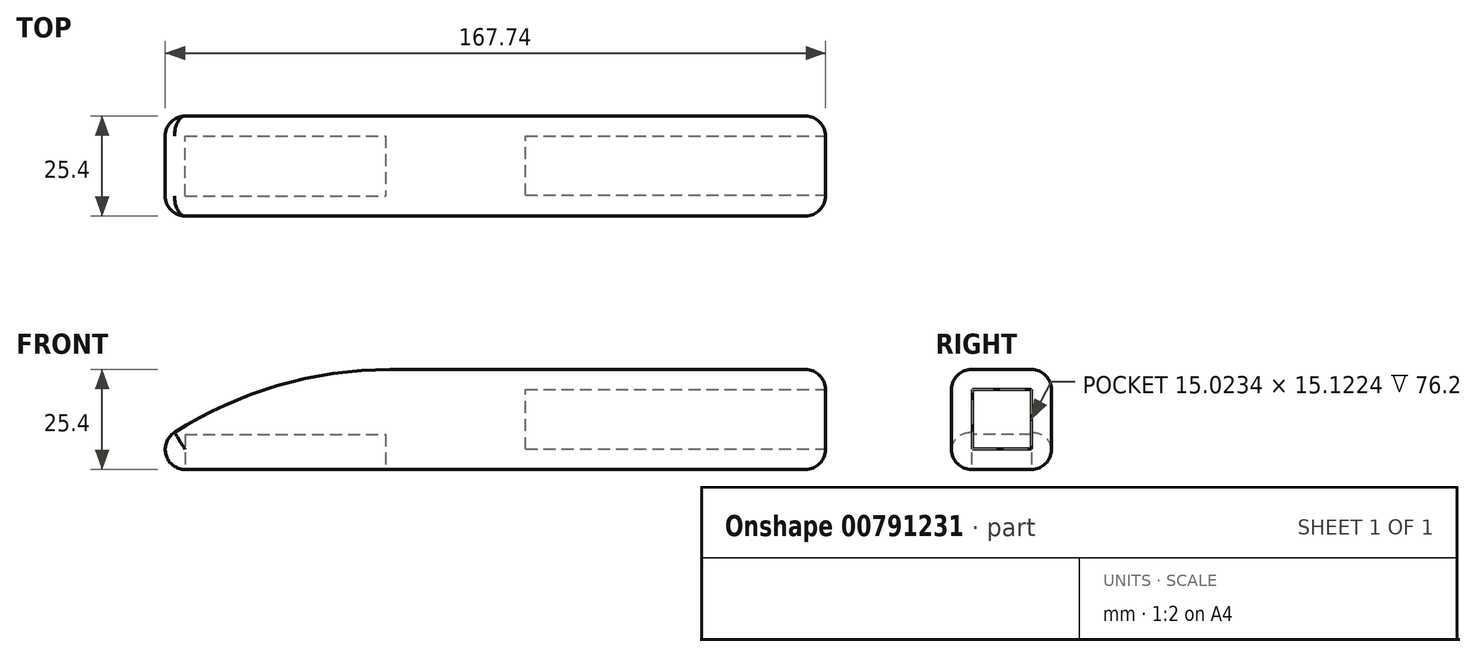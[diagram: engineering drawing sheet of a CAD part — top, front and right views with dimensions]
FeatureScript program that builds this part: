
annotation { "Feature Type Name" : "Feature", "Feature Type Description" : "" }
export const myFeature = defineFeature(function(context is Context, id is Id, definition is map)
    precondition{}
    {
        {
            var Q0;
            Q0=qCreatedBy(makeId("Top.planeOp"),FACE);
            var sketch = newSketch(context, id + "F0", { "sketchPlane" : qUnion([Q0])});
            skLineSegment(sketch, "E0.bottom", {"start": v(-85.74, 12.7) * mm, "end": v(92.06, 12.7) * mm});
            skLineSegment(sketch, "E0.top", {"start": v(-85.74, -12.7) * mm, "end": v(92.06, -12.7) * mm});
            skLineSegment(sketch, "E0.left", {"start": v(-85.74, 12.7) * mm, "end": v(-85.74, -12.7) * mm});
            skLineSegment(sketch, "E0.right", {"start": v(92.06, 12.7) * mm, "end": v(92.06, -12.7) * mm});
            skPoint(sketch, "E0.middle", {"position": v(3.16, 0) * mm});
            skSolve(sketch);
        }
        {
            var Q0;
            Q0=makeQuery(id+"F0.imprint","IMPRINT",FACE,{"disambiguationData":[TD([[makeQuery(id+"F0.imprint","IMPRINT",EDGE,{"derivedFrom":sQuery(id+"F0.wireOp",EDGE,"E0.bottom")}),-1.0]])]});
            extrude(context, id + "F1", {"entities" : qUnion([Q0]), "depth" : 25.4 * mm, "offsetDistance" : 25.4 * mm});
        }
        {
            var Q0;
            Q0=makeQuery(id+"F1.opExtrude","CAP_EDGE",EDGE,{"disambiguationData":[OSD([sQuery(id+"F0.wireOp",EDGE,"E0.left")])],"isStart":false});
            fillet(context, id + "F2", {"entities" : qUnion([Q0]), "radius" : 101.6 * mm, "tangentPropagation" : true, "allowEdgeOverflow" : false});
        }
        {
            var Q0;
            Q0=makeQuery(id+"F2.opFillet","BLEND_EDGE",EDGE,{"blendedFrom":[makeQuery(id+"F1.opExtrude","CAP_EDGE",EDGE,{"disambiguationData":[OSD([sQuery(id+"F0.wireOp",EDGE,"E0.left")])],"isStart":false}),makeQuery(id+"F1.opExtrude","SWEPT_FACE",FACE,{"disambiguationData":[OSD([sQuery(id+"F0.wireOp",EDGE,"E0.top")])]})],"blendedInto":[makeQuery(id+"F1.opExtrude","SWEPT_FACE",FACE,{"disambiguationData":[OSD([sQuery(id+"F0.wireOp",EDGE,"E0.top")])]})]});
            var Q1;
            Q1=makeQuery(id+"F2.opFillet","BLEND_EDGE",EDGE,{"blendedFrom":[makeQuery(id+"F1.opExtrude","CAP_EDGE",EDGE,{"disambiguationData":[OSD([sQuery(id+"F0.wireOp",EDGE,"E0.left")])],"isStart":false}),makeQuery(id+"F1.opExtrude","SWEPT_FACE",FACE,{"disambiguationData":[OSD([sQuery(id+"F0.wireOp",EDGE,"E0.bottom")])]})],"blendedInto":[makeQuery(id+"F1.opExtrude","SWEPT_FACE",FACE,{"disambiguationData":[OSD([sQuery(id+"F0.wireOp",EDGE,"E0.bottom")])]})]});
            fillet(context, id + "F3", {"entities" : qUnion([Q0, Q1]), "radius" : 5.08 * mm, "tangentPropagation" : true, "allowEdgeOverflow" : false});
        }
        {
            var Q0;
            Q0=makeQuery(id+"F1.opExtrude","SWEPT_FACE",FACE,{"disambiguationData":[OSD([sQuery(id+"F0.wireOp",EDGE,"E0.right")])]});
            var sketch = newSketch(context, id + "F4", { "sketchPlane" : qUnion([Q0])});
            skLineSegment(sketch, "E1.bottom", {"start": v(-7.4, 5.2) * mm, "end": v(7.62, 5.2) * mm});
            skLineSegment(sketch, "E1.top", {"start": v(-7.4, 20.32) * mm, "end": v(7.62, 20.32) * mm});
            skLineSegment(sketch, "E1.left", {"start": v(-7.4, 5.2) * mm, "end": v(-7.4, 20.32) * mm});
            skLineSegment(sketch, "E1.right", {"start": v(7.62, 5.2) * mm, "end": v(7.62, 20.32) * mm});
            skSolve(sketch);
        }
        {
            var Q0;
            Q0=makeQuery(id+"F4.imprint","IMPRINT",FACE,{"disambiguationData":[TD([[makeQuery(id+"F4.imprint","IMPRINT",EDGE,{"derivedFrom":sQuery(id+"F4.wireOp",EDGE,"E1.bottom")}),1.0]])]});
            extrude(context, id + "F5", {"entities" : qUnion([Q0]), "operationType" : NewBodyOperationType.REMOVE, "oppositeDirection" : true, "depth" : 76.2 * mm, "offsetDistance" : 25.4 * mm});
        }
        {
            var Q0;
            Q0=makeQuery(id+"F1.opExtrude","CAP_EDGE",EDGE,{"disambiguationData":[OSD([sQuery(id+"F0.wireOp",EDGE,"E0.right")])],"isStart":false});
            var Q1;
            Q1=makeQuery(id+"F1.opExtrude","CAP_EDGE",EDGE,{"disambiguationData":[OSD([sQuery(id+"F0.wireOp",EDGE,"E0.right")])],"isStart":true});
            fillet(context, id + "F6", {"entities" : qUnion([Q0, Q1]), "radius" : 5.08 * mm, "tangentPropagation" : true, "allowEdgeOverflow" : false});
        }
        {
            var Q0;
            Q0=makeQuery(id+"F1.opExtrude","CAP_EDGE",EDGE,{"disambiguationData":[OSD([sQuery(id+"F0.wireOp",EDGE,"E0.top")])],"isStart":true});
            var Q1;
            Q1=makeQuery(id+"F1.opExtrude","CAP_EDGE",EDGE,{"disambiguationData":[OSD([sQuery(id+"F0.wireOp",EDGE,"E0.bottom")])],"isStart":true});
            fillet(context, id + "F7", {"entities" : qUnion([Q0, Q1]), "radius" : 5.08 * mm, "tangentPropagation" : true, "allowEdgeOverflow" : false});
        }
        {
            var Q0;
            Q0=makeQuery(id+"F1.opExtrude","CAP_FACE",FACE,{"disambiguationData":[OSD([sQuery(id+"F0.wireOp",EDGE,"E0.bottom"),sQuery(id+"F0.wireOp",EDGE,"E0.top"),sQuery(id+"F0.wireOp",EDGE,"E0.left"),sQuery(id+"F0.wireOp",EDGE,"E0.right")])],"isStart":true});
            var sketch = newSketch(context, id + "F8", { "sketchPlane" : qUnion([Q0])});
            skLineSegment(sketch, "E2", {"start": v(-19.69, -7.62) * mm, "end": v(-19.69, 7.62) * mm});
            skSolve(sketch);
        }
        {
            var Q0;
            {var subQ0=sQuery(id+"F8.wireOp",EDGE,"E2");Q0=makeQuery(id+"F8.imprint","IMPRINT",FACE,{"disambiguationData":[TD([[makeQuery(id+"F8.imprint","IMPRINT",EDGE,{"derivedFrom":subQ0}),1.0]])]});}
            extrude(context, id + "F9", {"entities" : qUnion([Q0]), "operationType" : NewBodyOperationType.REMOVE, "oppositeDirection" : true, "depth" : 8.9 * mm, "offsetDistance" : 25.4 * mm});
        }
        {
            var Q0;
            Q0=makeQuery(id+"F1.opExtrude","SWEPT_FACE",FACE,{"disambiguationData":[OSD([sQuery(id+"F0.wireOp",EDGE,"E0.top")])]});
            var sketch = newSketch(context, id + "F10", { "sketchPlane" : qUnion([Q0])});
            skLineSegment(sketch, "E3", {"start": v(-30.42, 18.15) * mm, "end": v(-30.42, 7.54) * mm});
            skLineSegment(sketch, "E4", {"start": v(-25.14, 18.15) * mm, "end": v(-25.14, 13.62) * mm});
            skLineSegment(sketch, "E5", {"start": v(-25.14, 13.62) * mm, "end": v(-30.42, 13.62) * mm});
            skSolve(sketch);
        }
    });
